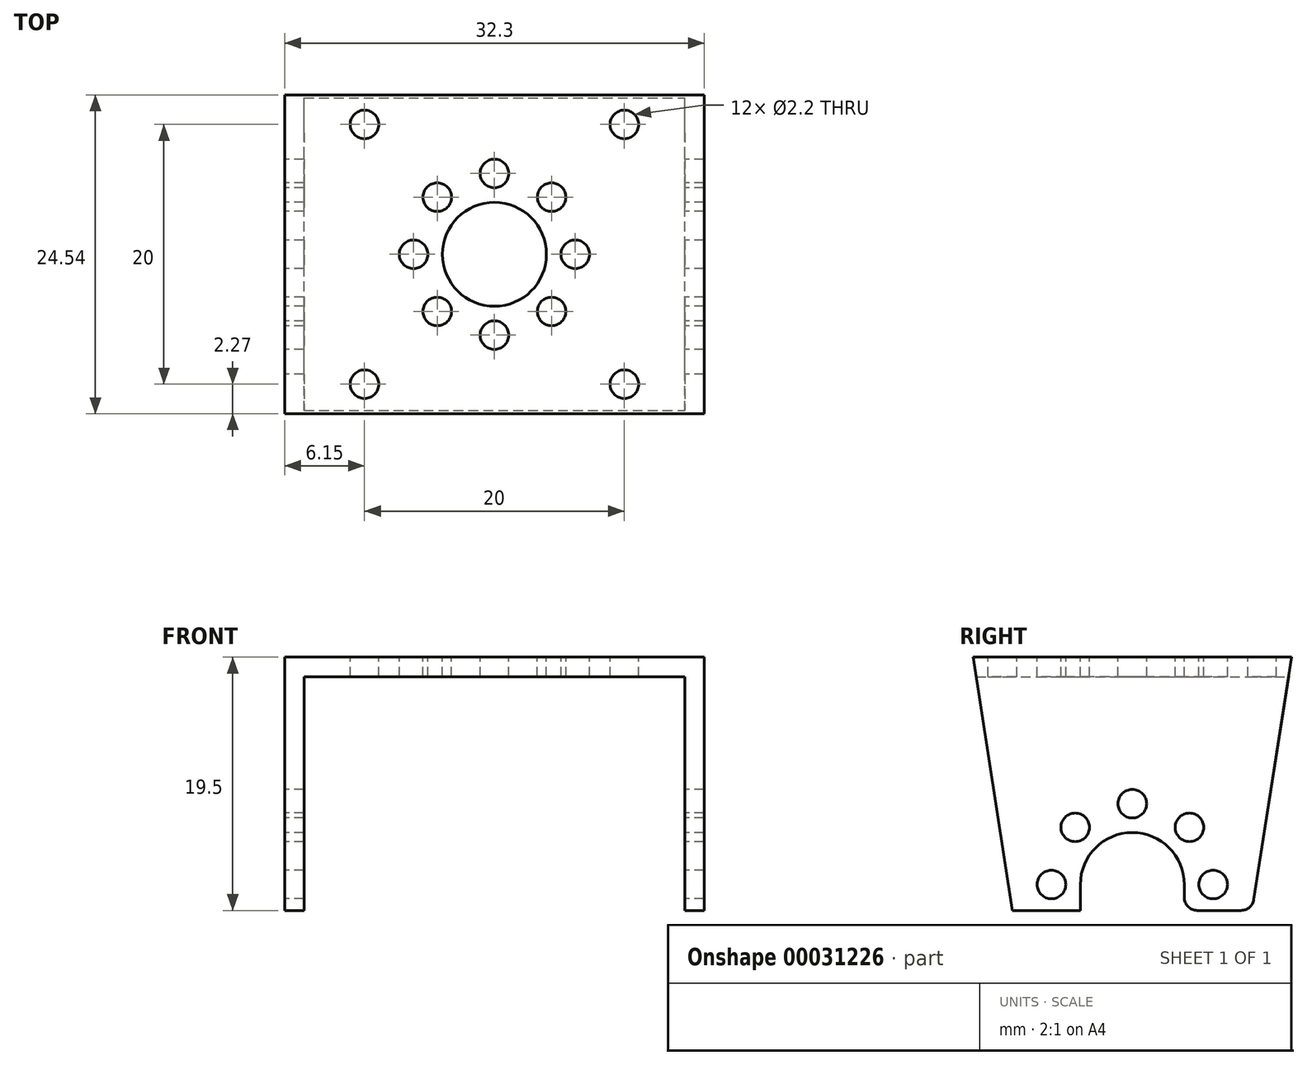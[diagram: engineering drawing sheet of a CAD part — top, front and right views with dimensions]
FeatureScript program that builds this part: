
annotation { "Feature Type Name" : "Feature", "Feature Type Description" : "" }
export const myFeature = defineFeature(function(context is Context, id is Id, definition is map)
    precondition{}
    {
        {
            var Q0;
            Q0=qCreatedBy(makeId("Front.planeOp"),FACE);
            var sketch = newSketch(context, id + "F0", { "sketchPlane" : qUnion([Q0])});
            skLineSegment(sketch, "E0.bottom", {"start": v(0, 0) * mm, "end": v(1.5, 0) * mm});
            skLineSegment(sketch, "E0.top", {"start": v(0, 19.5) * mm, "end": v(32.3, 19.5) * mm});
            skLineSegment(sketch, "E0.left", {"start": v(0, 0) * mm, "end": v(0, 19.5) * mm});
            skLineSegment(sketch, "E0.right", {"start": v(32.3, 0) * mm, "end": v(32.3, 19.5) * mm});
            skLineSegment(sketch, "E1.top", {"start": v(1.5, 18) * mm, "end": v(30.8, 18) * mm});
            skLineSegment(sketch, "E1.left", {"start": v(1.5, 0) * mm, "end": v(1.5, 18) * mm});
            skLineSegment(sketch, "E1.right", {"start": v(30.8, 0) * mm, "end": v(30.8, 18) * mm});
            skLineSegment(sketch, "E2.trimOffspring", {"start": v(30.8, 0) * mm, "end": v(32.3, 0) * mm});
            skSolve(sketch);
        }
        {
            var Q0;
            Q0=qSketchRegion(id+"F0",true);
            extrude(context, id + "F1", {"entities" : qUnion([Q0]), "depth" : 25 * mm});
        }
        {
            var Q0;
            Q0=makeQuery(id+"F1.opExtrude","SWEPT_FACE",FACE,{"disambiguationData":[OSD([sQuery(id+"F0.wireOp",EDGE,"E0.left")])]});
            var sketch = newSketch(context, id + "F2", { "sketchPlane" : qUnion([Q0])});
            skArc(sketch, "E3", {"start": v(16.5, 2) * mm, "mid": v(12.5, 6) * mm, "end": v(8.5, 2) * mm});
            skCircle(sketch, "E4", {"center": v(18.72, 2) * mm, "radius": 1.1 * mm});
            skCircle(sketch, "E5.1.0", {"center": v(16.9, 6.4) * mm, "radius": 1.1 * mm});
            skCircle(sketch, "E5.2.0", {"center": v(12.5, 8.22) * mm, "radius": 1.1 * mm});
            skCircle(sketch, "E5.3.0", {"center": v(8.1, 6.4) * mm, "radius": 1.1 * mm});
            skCircle(sketch, "E5.4.0", {"center": v(6.28, 2) * mm, "radius": 1.1 * mm});
            skLineSegment(sketch, "E6", {"start": v(8.5, 2) * mm, "end": v(8.5, 0) * mm});
            skLineSegment(sketch, "E7", {"start": v(16.5, 2) * mm, "end": v(16.5, 0) * mm});
            skLineSegment(sketch, "E8", {"start": v(8.5, 0) * mm, "end": v(16.5, 0) * mm});
            skLineSegment(sketch, "E9", {"start": v(12.5, 19.5) * mm, "end": v(12.5, 0) * mm, "construction": true});
            skPoint(sketch, "E10", {"position": v(12.5, 0) * mm});
            skLineSegment(sketch, "E11", {"start": v(3.28, 0) * mm, "end": v(0, 21) * mm});
            skLineSegment(sketch, "E12", {"start": v(3.28, 0) * mm, "end": v(0, 0) * mm});
            skLineSegment(sketch, "E13", {"start": v(0, 0) * mm, "end": v(0, 21) * mm});
            skLineSegment(sketch, "E14.MirrorCS", {"start": v(25, 0) * mm, "end": v(25, 21) * mm});
            skLineSegment(sketch, "E15.MirrorCS", {"start": v(21.72, 0) * mm, "end": v(25, 21) * mm});
            skLineSegment(sketch, "E16.MirrorCS", {"start": v(21.72, 0) * mm, "end": v(25, 0) * mm});
            skSolve(sketch);
        }
        {
            var Q0;
            Q0=qSketchRegion(id+"F2",true);
            extrude(context, id + "F3", {"entities" : qUnion([Q0]), "operationType" : NewBodyOperationType.REMOVE, "endBound" : BoundingType.THROUGH_ALL, "oppositeDirection" : true, "depth" : 25 * mm});
        }
        {
            var Q0;
            Q0=makeQuery(id+"F1.opExtrude","SWEPT_FACE",FACE,{"disambiguationData":[OSD([sQuery(id+"F0.wireOp",EDGE,"E0.top")])]});
            var sketch = newSketch(context, id + "F4", { "sketchPlane" : qUnion([Q0])});
            skLineSegment(sketch, "E17", {"start": v(16.15, -0.23) * mm, "end": v(16.15, -24.77) * mm, "construction": true});
            skLineSegment(sketch, "E18", {"start": v(0, -12.5) * mm, "end": v(32.3, -12.5) * mm, "construction": true});
            skCircle(sketch, "E19", {"center": v(6.15, -2.5) * mm, "radius": 1.1 * mm});
            skCircle(sketch, "E20.MirrorC", {"center": v(26.15, -2.5) * mm, "radius": 1.1 * mm});
            skCircle(sketch, "E21.MirrorC", {"center": v(6.15, -22.5) * mm, "radius": 1.1 * mm});
            skCircle(sketch, "E22.MirrorC", {"center": v(26.15, -22.5) * mm, "radius": 1.1 * mm});
            skCircle(sketch, "E23", {"center": v(16.15, -12.5) * mm, "radius": 4 * mm});
            skLineSegment(sketch, "E24.bottom", {"start": v(20.55, -16.9) * mm, "end": v(11.75, -16.9) * mm, "construction": true});
            skLineSegment(sketch, "E24.top", {"start": v(20.55, -8.1) * mm, "end": v(11.75, -8.1) * mm, "construction": true});
            skLineSegment(sketch, "E24.left", {"start": v(20.55, -16.9) * mm, "end": v(20.55, -8.1) * mm, "construction": true});
            skLineSegment(sketch, "E24.right", {"start": v(11.75, -16.9) * mm, "end": v(11.75, -8.1) * mm, "construction": true});
            skCircle(sketch, "E25", {"center": v(11.75, -8.1) * mm, "radius": 1.1 * mm});
            skCircle(sketch, "E26.1.0", {"center": v(9.93, -12.5) * mm, "radius": 1.1 * mm});
            skCircle(sketch, "E26.2.0", {"center": v(11.75, -16.9) * mm, "radius": 1.1 * mm});
            skCircle(sketch, "E26.3.0", {"center": v(16.15, -18.72) * mm, "radius": 1.1 * mm});
            skCircle(sketch, "E27.1.4.0", {"center": v(20.55, -16.9) * mm, "radius": 1.1 * mm});
            skCircle(sketch, "E27.1.5.0", {"center": v(22.37, -12.5) * mm, "radius": 1.1 * mm});
            skCircle(sketch, "E27.1.6.0", {"center": v(20.55, -8.1) * mm, "radius": 1.1 * mm});
            skCircle(sketch, "E27.1.7.0", {"center": v(16.15, -6.28) * mm, "radius": 1.1 * mm});
            skLineSegment(sketch, "E28.0", {"start": v(0, -24.77) * mm, "end": v(0, -0.23) * mm, "construction": true});
            skLineSegment(sketch, "E29.0", {"start": v(0, -0.23) * mm, "end": v(32.3, -0.23) * mm, "construction": true});
            skLineSegment(sketch, "E30.0", {"start": v(32.3, -24.77) * mm, "end": v(32.3, -0.23) * mm, "construction": true});
            skLineSegment(sketch, "E31.0", {"start": v(0, -24.77) * mm, "end": v(32.3, -24.77) * mm, "construction": true});
            skPoint(sketch, "E32", {"position": v(16.15, -24.77) * mm});
            skPoint(sketch, "E33", {"position": v(16.15, -0.23) * mm});
            skSolve(sketch);
        }
        {
            var Q0;
            Q0 = qSketchRegion(id + "F4", true);
            extrude(context, id + "F5", {"entities" : qUnion([Q0]), "operationType" : NewBodyOperationType.REMOVE, "endBound" : BoundingType.UP_TO_NEXT, "oppositeDirection" : true, "depth" : 25 * mm});
        }
        {
            var Q0;
            Q0=makeQuery(id+"F3.boolean.opBoolean","COPY",EDGE,{"disambiguationData":[OD(0.0)],"derivedFrom":makeQuery(id+"F3.opExtrude","SWEPT_EDGE",EDGE,{"disambiguationData":[OSD([sQuery(id+"F0.wireOp",EDGE,"E0.bottom"),sQuery(id+"F0.wireOp",EDGE,"E0.left"),sQuery(id+"F2.wireOp",EDGE,"E11"),sQuery(id+"F2.wireOp",EDGE,"E12")])]})});
            var Q1;
            Q1=makeQuery(id+"F3.boolean.opBoolean","COPY",EDGE,{"disambiguationData":[OD(0.0)],"derivedFrom":makeQuery(id+"F3.opExtrude","SWEPT_EDGE",EDGE,{"disambiguationData":[OSD([sQuery(id+"F0.wireOp",EDGE,"E0.bottom"),sQuery(id+"F0.wireOp",EDGE,"E0.left"),sQuery(id+"F2.wireOp",EDGE,"E6"),sQuery(id+"F2.wireOp",EDGE,"E8")])]})});
            var Q2;
            Q2=makeQuery(id+"F3.boolean.opBoolean","COPY",EDGE,{"disambiguationData":[OD(0.0)],"derivedFrom":makeQuery(id+"F3.opExtrude","SWEPT_EDGE",EDGE,{"disambiguationData":[OSD([sQuery(id+"F0.wireOp",EDGE,"E0.bottom"),sQuery(id+"F0.wireOp",EDGE,"E0.left"),sQuery(id+"F2.wireOp",EDGE,"E7"),sQuery(id+"F2.wireOp",EDGE,"E8")])]})});
            var Q3;
            Q3=makeQuery(id+"F3.boolean.opBoolean","COPY",EDGE,{"disambiguationData":[OD(0.0)],"derivedFrom":makeQuery(id+"F3.opExtrude","SWEPT_EDGE",EDGE,{"disambiguationData":[OSD([sQuery(id+"F0.wireOp",EDGE,"E0.bottom"),sQuery(id+"F0.wireOp",EDGE,"E0.left"),sQuery(id+"F2.wireOp",EDGE,"E15.MirrorCS"),sQuery(id+"F2.wireOp",EDGE,"E16.MirrorCS")])]})});
            var Q4;
            Q4=makeQuery(id+"F3.boolean.opBoolean","COPY",EDGE,{"disambiguationData":[OD(1.0)],"derivedFrom":makeQuery(id+"F3.opExtrude","SWEPT_EDGE",EDGE,{"disambiguationData":[OSD([sQuery(id+"F0.wireOp",EDGE,"E0.bottom"),sQuery(id+"F0.wireOp",EDGE,"E0.left"),sQuery(id+"F2.wireOp",EDGE,"E11"),sQuery(id+"F2.wireOp",EDGE,"E12")])]})});
            var Q5;
            Q5=makeQuery(id+"F3.boolean.opBoolean","COPY",EDGE,{"disambiguationData":[OD(1.0)],"derivedFrom":makeQuery(id+"F3.opExtrude","SWEPT_EDGE",EDGE,{"disambiguationData":[OSD([sQuery(id+"F0.wireOp",EDGE,"E0.bottom"),sQuery(id+"F0.wireOp",EDGE,"E0.left"),sQuery(id+"F2.wireOp",EDGE,"E6"),sQuery(id+"F2.wireOp",EDGE,"E8")])]})});
            var Q6;
            Q6=makeQuery(id+"F3.boolean.opBoolean","COPY",EDGE,{"disambiguationData":[OD(1.0)],"derivedFrom":makeQuery(id+"F3.opExtrude","SWEPT_EDGE",EDGE,{"disambiguationData":[OSD([sQuery(id+"F0.wireOp",EDGE,"E0.bottom"),sQuery(id+"F0.wireOp",EDGE,"E0.left"),sQuery(id+"F2.wireOp",EDGE,"E7"),sQuery(id+"F2.wireOp",EDGE,"E8")])]})});
            var Q7;
            Q7=makeQuery(id+"F3.boolean.opBoolean","COPY",EDGE,{"disambiguationData":[OD(1.0)],"derivedFrom":makeQuery(id+"F3.opExtrude","SWEPT_EDGE",EDGE,{"disambiguationData":[OSD([sQuery(id+"F0.wireOp",EDGE,"E0.bottom"),sQuery(id+"F0.wireOp",EDGE,"E0.left"),sQuery(id+"F2.wireOp",EDGE,"E15.MirrorCS"),sQuery(id+"F2.wireOp",EDGE,"E16.MirrorCS")])]})});
            fillet(context, id + "F6", {"entities" : qUnion([Q0, Q1, Q2, Q3, Q4, Q5, Q6, Q7]), "radius" : 1 * mm, "tangentPropagation" : true, "allowEdgeOverflow" : false});
        }
    });
